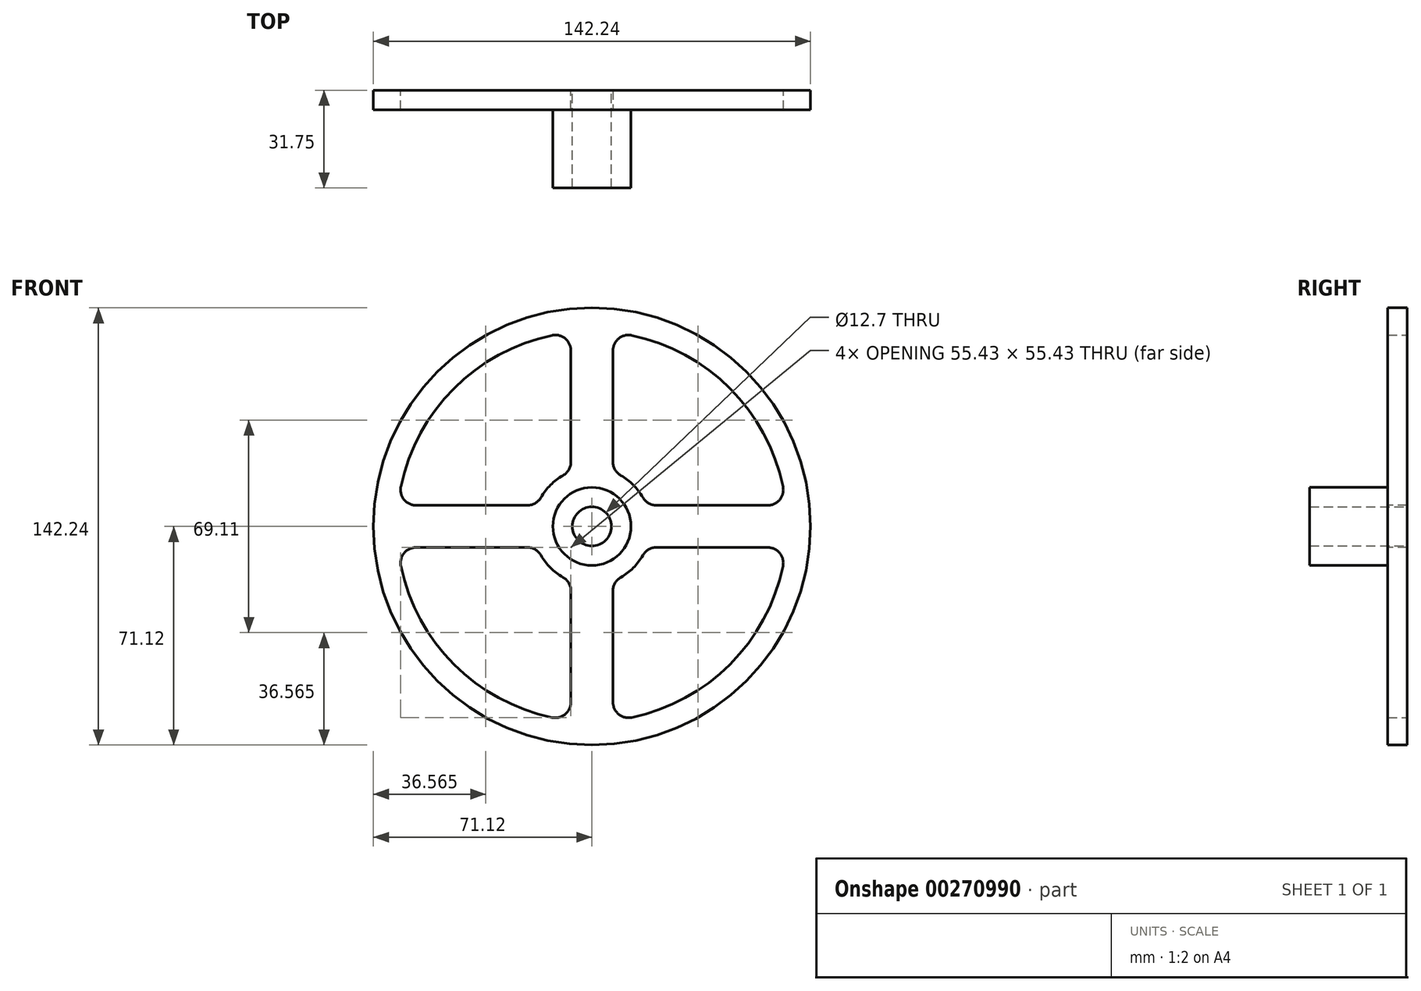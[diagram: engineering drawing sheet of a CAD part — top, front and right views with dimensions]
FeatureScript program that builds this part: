
annotation { "Feature Type Name" : "Feature", "Feature Type Description" : "" }
export const myFeature = defineFeature(function(context is Context, id is Id, definition is map)
    precondition{}
    {
        {
            var Q0;
            Q0=qCreatedBy(makeId("Front.planeOp"),FACE);
            var sketch = newSketch(context, id + "F0", { "sketchPlane" : qUnion([Q0])});
            skCircle(sketch, "E0", {"center": v(0, 0) * mm, "radius": 71.12 * mm});
            skArc(sketch, "E1", {"start": v(63.13, 6.84) * mm, "mid": v(44.9, 44.9) * mm, "end": v(6.84, 63.13) * mm});
            skCircle(sketch, "E2", {"center": v(0, 0) * mm, "radius": 12.7 * mm});
            skCircle(sketch, "E3", {"center": v(0, 0) * mm, "radius": 6.35 * mm});
            skArc(sketch, "E4", {"start": v(-6.84, 17.78) * mm, "mid": v(-13.47, 13.47) * mm, "end": v(-17.78, 6.84) * mm});
            skLineSegment(sketch, "E5", {"start": v(6.84, 63.13) * mm, "end": v(6.84, 17.78) * mm});
            skLineSegment(sketch, "E6", {"start": v(17.78, 6.84) * mm, "end": v(63.13, 6.84) * mm});
            skLineSegment(sketch, "E7.1.0", {"start": v(-63.13, 6.84) * mm, "end": v(-17.78, 6.84) * mm});
            skArc(sketch, "E7.1.1", {"start": v(-6.84, 63.13) * mm, "mid": v(-44.9, 44.9) * mm, "end": v(-63.13, 6.84) * mm});
            skLineSegment(sketch, "E7.1.2", {"start": v(-6.84, 17.78) * mm, "end": v(-6.84, 63.13) * mm});
            skLineSegment(sketch, "E7.2.0", {"start": v(-6.84, -63.13) * mm, "end": v(-6.84, -17.78) * mm});
            skArc(sketch, "E7.2.1", {"start": v(-63.13, -6.84) * mm, "mid": v(-44.9, -44.9) * mm, "end": v(-6.84, -63.13) * mm});
            skLineSegment(sketch, "E7.2.2", {"start": v(-17.78, -6.84) * mm, "end": v(-63.13, -6.84) * mm});
            skLineSegment(sketch, "E7.3.0", {"start": v(63.13, -6.84) * mm, "end": v(17.78, -6.84) * mm});
            skArc(sketch, "E7.3.1", {"start": v(6.84, -63.13) * mm, "mid": v(44.9, -44.9) * mm, "end": v(63.13, -6.84) * mm});
            skLineSegment(sketch, "E7.3.2", {"start": v(6.84, -17.78) * mm, "end": v(6.84, -63.13) * mm});
            skArc(sketch, "E8.trimOffspring", {"start": v(6.84, -17.78) * mm, "mid": v(13.47, -13.47) * mm, "end": v(17.78, -6.84) * mm});
            skArc(sketch, "E9.trimOffspring", {"start": v(-17.78, -6.84) * mm, "mid": v(-13.47, -13.47) * mm, "end": v(-6.84, -17.78) * mm});
            skArc(sketch, "E10.trimOffspring", {"start": v(17.78, 6.84) * mm, "mid": v(13.47, 13.47) * mm, "end": v(6.84, 17.78) * mm});
            skSolve(sketch);
        }
        {
            var Q0;
            Q0 = qSketchRegion(id + "F0", true);
            var Q1;
            Q1=makeQuery(id+"F0.imprint","IMPRINT",FACE,{"disambiguationData":[TD([[makeQuery(id+"F0.imprint","IMPRINT",EDGE,{"derivedFrom":sQuery(id+"F0.wireOp",EDGE,"E2")}),1.0]])]});
            extrude(context, id + "F1", {"entities" : qUnion([Q0, Q1]), "depth" : 6.35 * mm});
        }
        {
            var Q0;
            Q0=makeQuery(id+"F1.opExtrude","CAP_FACE",FACE,{"disambiguationData":[OSD([sQuery(id+"F0.wireOp",EDGE,"E0"),sQuery(id+"F0.wireOp",EDGE,"E1"),sQuery(id+"F0.wireOp",EDGE,"E2"),sQuery(id+"F0.wireOp",EDGE,"E4"),sQuery(id+"F0.wireOp",EDGE,"E5"),sQuery(id+"F0.wireOp",EDGE,"E6"),sQuery(id+"F0.wireOp",EDGE,"E7.1.0"),sQuery(id+"F0.wireOp",EDGE,"E7.1.1"),sQuery(id+"F0.wireOp",EDGE,"E7.1.2"),sQuery(id+"F0.wireOp",EDGE,"E7.2.0"),sQuery(id+"F0.wireOp",EDGE,"E7.2.1"),sQuery(id+"F0.wireOp",EDGE,"E7.2.2"),sQuery(id+"F0.wireOp",EDGE,"E7.3.0"),sQuery(id+"F0.wireOp",EDGE,"E7.3.1"),sQuery(id+"F0.wireOp",EDGE,"E7.3.2"),sQuery(id+"F0.wireOp",EDGE,"E8.trimOffspring"),sQuery(id+"F0.wireOp",EDGE,"E9.trimOffspring"),sQuery(id+"F0.wireOp",EDGE,"E10.trimOffspring")])],"isStart":false});
            var sketch = newSketch(context, id + "F2", { "sketchPlane" : qUnion([Q0])});
            skCircle(sketch, "E11", {"center": v(0, 0) * mm, "radius": 12.7 * mm});
            skSolve(sketch);
        }
        {
            var Q0;
            Q0=makeQuery(id+"F2.imprint","IMPRINT",FACE,{"disambiguationData":[TD([[makeQuery(id+"F2.imprint","IMPRINT",EDGE,{"derivedFrom":sQuery(id+"F2.wireOp",EDGE,"E11")}),1.0]])]});
            extrude(context, id + "F3", {"entities" : qUnion([Q0]), "operationType" : NewBodyOperationType.ADD, "depth" : 25.4 * mm});
        }
        {
            var Q0;
            Q0=makeQuery(id+"F1.opExtrude","SWEPT_EDGE",EDGE,{"disambiguationData":[OSD([sQuery(id+"F0.wireOp",EDGE,"E1"),sQuery(id+"F0.wireOp",EDGE,"E5")])]});
            var Q1;
            Q1=makeQuery(id+"F1.opExtrude","SWEPT_EDGE",EDGE,{"disambiguationData":[OSD([sQuery(id+"F0.wireOp",EDGE,"E5"),sQuery(id+"F0.wireOp",EDGE,"E10.trimOffspring")])]});
            var Q2;
            Q2=makeQuery(id+"F1.opExtrude","SWEPT_EDGE",EDGE,{"disambiguationData":[OSD([sQuery(id+"F0.wireOp",EDGE,"E6"),sQuery(id+"F0.wireOp",EDGE,"E10.trimOffspring")])]});
            var Q3;
            Q3=makeQuery(id+"F1.opExtrude","SWEPT_EDGE",EDGE,{"disambiguationData":[OSD([sQuery(id+"F0.wireOp",EDGE,"E1"),sQuery(id+"F0.wireOp",EDGE,"E6")])]});
            var Q4;
            Q4=makeQuery(id+"F1.opExtrude","SWEPT_EDGE",EDGE,{"disambiguationData":[OSD([sQuery(id+"F0.wireOp",EDGE,"E7.3.0"),sQuery(id+"F0.wireOp",EDGE,"E8.trimOffspring")])]});
            var Q5;
            Q5=makeQuery(id+"F1.opExtrude","SWEPT_EDGE",EDGE,{"disambiguationData":[OSD([sQuery(id+"F0.wireOp",EDGE,"E7.3.2"),sQuery(id+"F0.wireOp",EDGE,"E8.trimOffspring")])]});
            var Q6;
            Q6=makeQuery(id+"F1.opExtrude","SWEPT_EDGE",EDGE,{"disambiguationData":[OSD([sQuery(id+"F0.wireOp",EDGE,"E7.3.0"),sQuery(id+"F0.wireOp",EDGE,"E7.3.1")])]});
            var Q7;
            Q7=makeQuery(id+"F1.opExtrude","SWEPT_EDGE",EDGE,{"disambiguationData":[OSD([sQuery(id+"F0.wireOp",EDGE,"E7.3.1"),sQuery(id+"F0.wireOp",EDGE,"E7.3.2")])]});
            var Q8;
            Q8=makeQuery(id+"F1.opExtrude","SWEPT_EDGE",EDGE,{"disambiguationData":[OSD([sQuery(id+"F0.wireOp",EDGE,"E7.2.0"),sQuery(id+"F0.wireOp",EDGE,"E7.2.1")])]});
            var Q9;
            Q9=makeQuery(id+"F1.opExtrude","SWEPT_EDGE",EDGE,{"disambiguationData":[OSD([sQuery(id+"F0.wireOp",EDGE,"E7.2.2"),sQuery(id+"F0.wireOp",EDGE,"E9.trimOffspring")])]});
            var Q10;
            Q10=makeQuery(id+"F1.opExtrude","SWEPT_EDGE",EDGE,{"disambiguationData":[OSD([sQuery(id+"F0.wireOp",EDGE,"E7.2.0"),sQuery(id+"F0.wireOp",EDGE,"E9.trimOffspring")])]});
            var Q11;
            Q11=makeQuery(id+"F1.opExtrude","SWEPT_EDGE",EDGE,{"disambiguationData":[OSD([sQuery(id+"F0.wireOp",EDGE,"E7.2.1"),sQuery(id+"F0.wireOp",EDGE,"E7.2.2")])]});
            var Q12;
            Q12=makeQuery(id+"F1.opExtrude","SWEPT_EDGE",EDGE,{"disambiguationData":[OSD([sQuery(id+"F0.wireOp",EDGE,"E4"),sQuery(id+"F0.wireOp",EDGE,"E7.1.0")])]});
            var Q13;
            Q13=makeQuery(id+"F1.opExtrude","SWEPT_EDGE",EDGE,{"disambiguationData":[OSD([sQuery(id+"F0.wireOp",EDGE,"E7.1.0"),sQuery(id+"F0.wireOp",EDGE,"E7.1.1")])]});
            var Q14;
            Q14=makeQuery(id+"F1.opExtrude","SWEPT_EDGE",EDGE,{"disambiguationData":[OSD([sQuery(id+"F0.wireOp",EDGE,"E7.1.1"),sQuery(id+"F0.wireOp",EDGE,"E7.1.2")])]});
            var Q15;
            Q15=makeQuery(id+"F1.opExtrude","SWEPT_EDGE",EDGE,{"disambiguationData":[OSD([sQuery(id+"F0.wireOp",EDGE,"E4"),sQuery(id+"F0.wireOp",EDGE,"E7.1.2")])]});
            fillet(context, id + "F4", {"entities" : qUnion([Q0, Q1, Q2, Q3, Q4, Q5, Q6, Q7, Q8, Q9, Q10, Q11, Q12, Q13, Q14, Q15]), "radius" : 5.08 * mm, "tangentPropagation" : true, "allowEdgeOverflow" : false});
        }
    });
